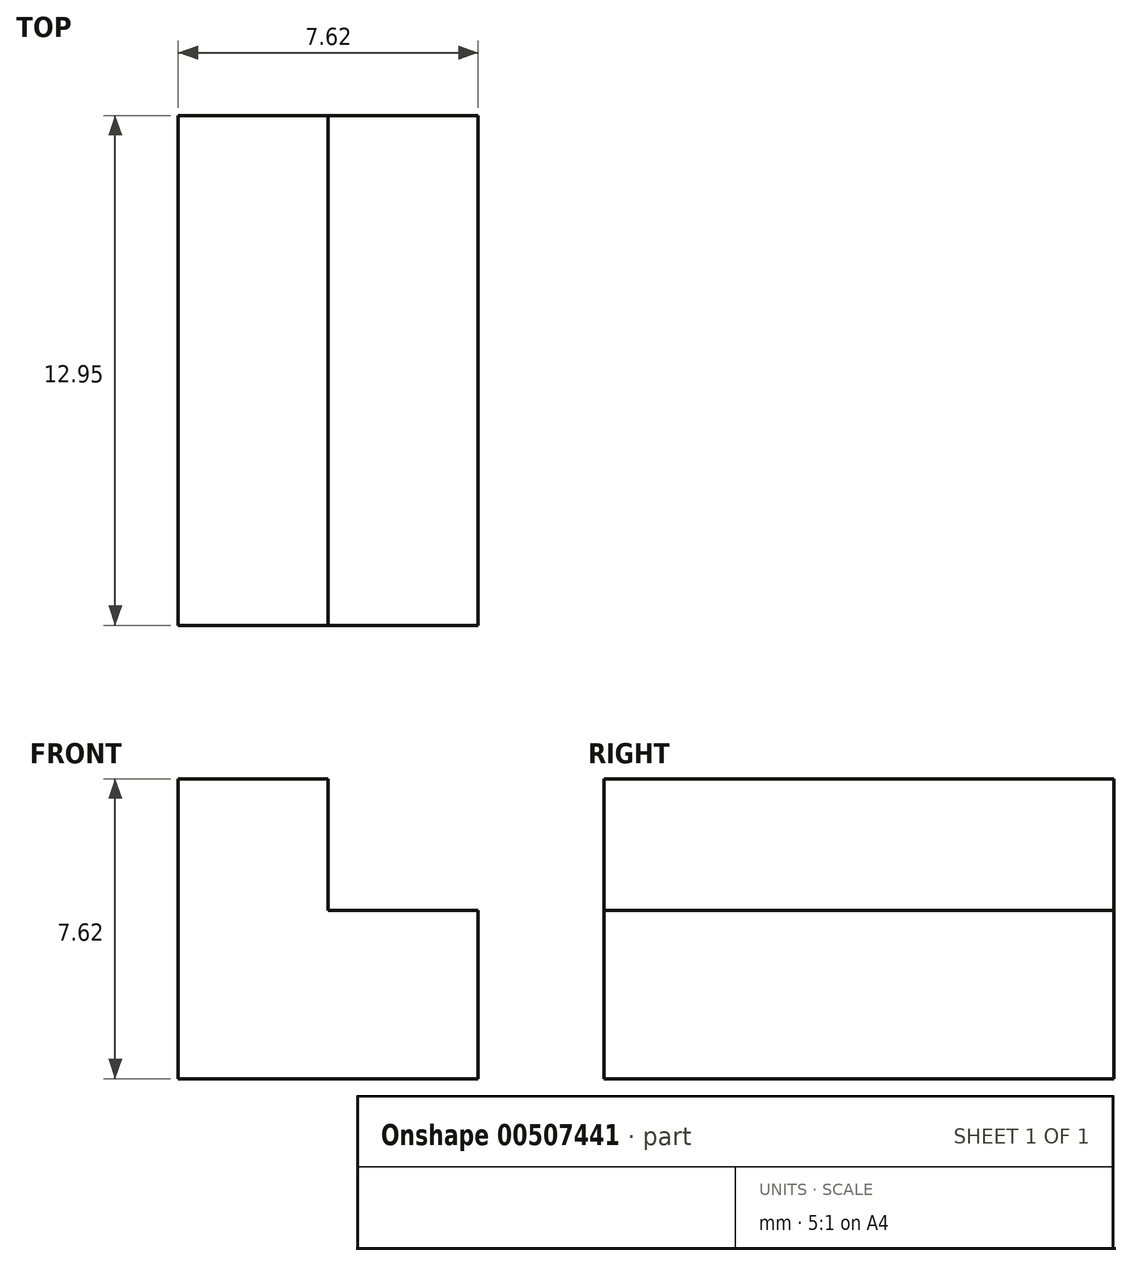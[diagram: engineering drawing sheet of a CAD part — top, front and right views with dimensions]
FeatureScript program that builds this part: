
annotation { "Feature Type Name" : "Feature", "Feature Type Description" : "" }
export const myFeature = defineFeature(function(context is Context, id is Id, definition is map)
    precondition{}
    {
        {
            var Q0;
            Q0=qCreatedBy(makeId("Front.planeOp"),FACE);
            var sketch = newSketch(context, id + "F0", { "sketchPlane" : qUnion([Q0])});
            skLineSegment(sketch, "E0", {"start": v(0, 0) * mm, "end": v(0, 7.62) * mm});
            skLineSegment(sketch, "E1", {"start": v(0, 7.62) * mm, "end": v(3.8, 7.62) * mm});
            skLineSegment(sketch, "E2", {"start": v(3.8, 7.62) * mm, "end": v(3.81, 4.27) * mm});
            skLineSegment(sketch, "E3", {"start": v(3.81, 4.27) * mm, "end": v(7.62, 4.27) * mm});
            skLineSegment(sketch, "E4", {"start": v(7.62, 4.27) * mm, "end": v(7.62, 0) * mm});
            skLineSegment(sketch, "E5", {"start": v(7.62, 0) * mm, "end": v(0, 0) * mm});
            skSolve(sketch);
        }
        {
            var Q0;
            Q0=makeQuery(id+"F0.imprint","IMPRINT",FACE,{"disambiguationData":[TD([[makeQuery(id+"F0.imprint","IMPRINT",EDGE,{"derivedFrom":sQuery(id+"F0.wireOp",EDGE,"E0")}),-1.0]])]});
            extrude(context, id + "F1", {"entities" : qUnion([Q0]), "depth" : 12.95 * mm});
        }
    });
